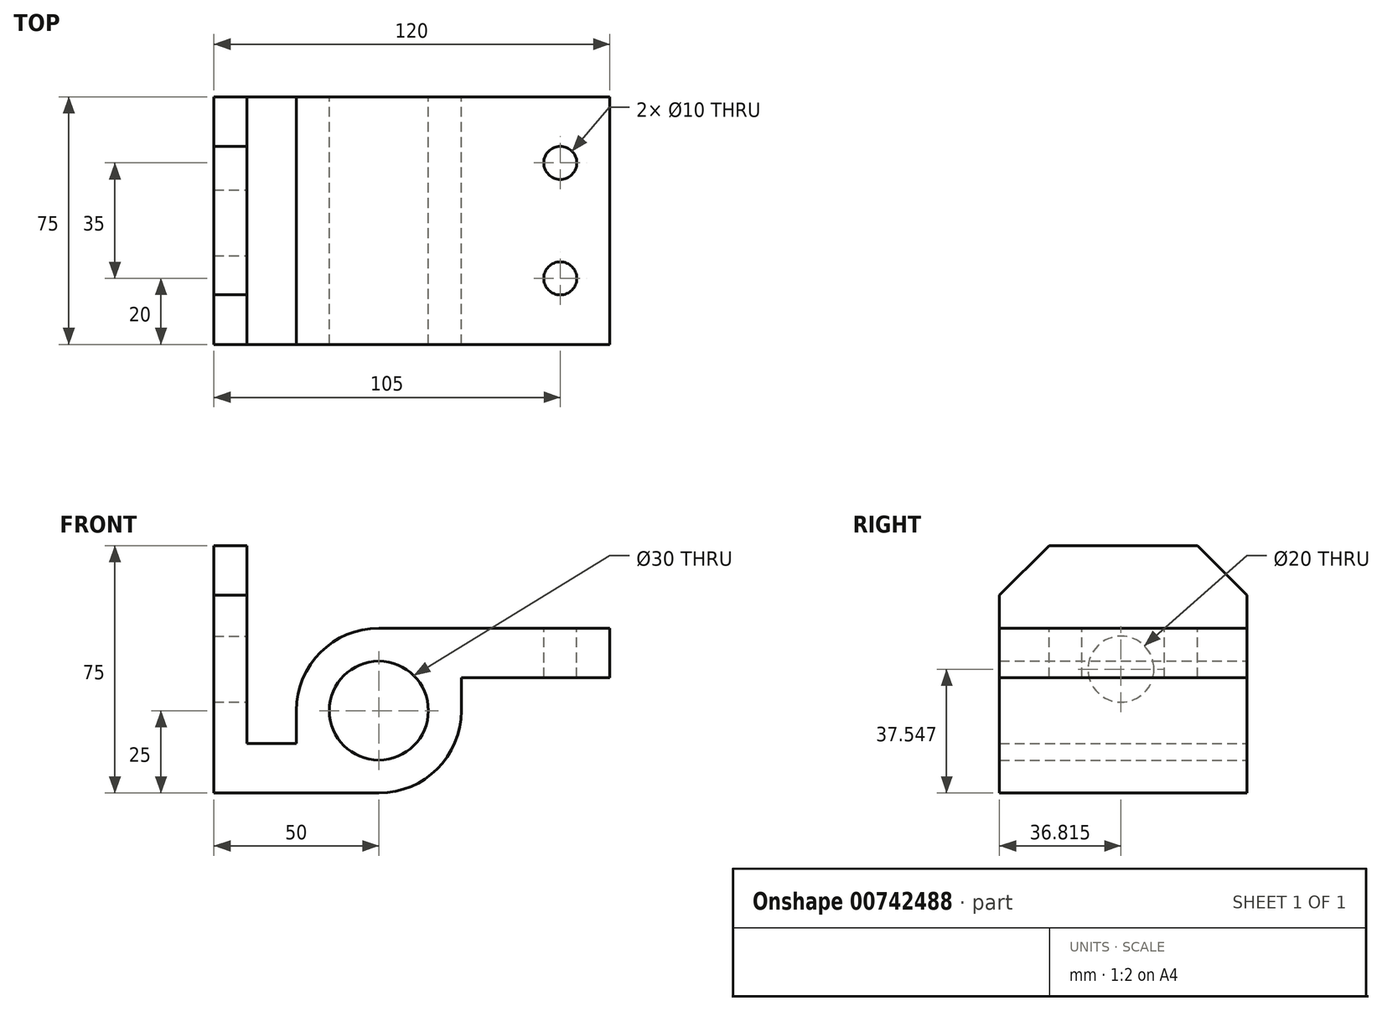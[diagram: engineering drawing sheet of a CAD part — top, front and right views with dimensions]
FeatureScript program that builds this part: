
annotation { "Feature Type Name" : "Feature", "Feature Type Description" : "" }
export const myFeature = defineFeature(function(context is Context, id is Id, definition is map)
    precondition{}
    {
        {
            var Q0;
            Q0=qCreatedBy(makeId("Front.planeOp"),FACE);
            var sketch = newSketch(context, id + "F0", { "sketchPlane" : qUnion([Q0])});
            skLineSegment(sketch, "E0", {"start": v(0, 0) * mm, "end": v(-50, 0) * mm});
            skLineSegment(sketch, "E1", {"start": v(-50, 0) * mm, "end": v(-50, 75) * mm});
            skLineSegment(sketch, "E2", {"start": v(-50, 75) * mm, "end": v(-40, 75) * mm});
            skLineSegment(sketch, "E3", {"start": v(-40, 75) * mm, "end": v(-40, 15) * mm});
            skLineSegment(sketch, "E4", {"start": v(-40, 15) * mm, "end": v(-25, 15) * mm});
            skLineSegment(sketch, "E5", {"start": v(0, 10) * mm, "end": v(0, 25) * mm});
            skArc(sketch, "E6", {"start": v(0, 0) * mm, "mid": v(17.68, 7.32) * mm, "end": v(25, 25) * mm});
            skCircle(sketch, "E7", {"center": v(0, 25) * mm, "radius": 15 * mm});
            skLineSegment(sketch, "E8", {"start": v(-25, 15) * mm, "end": v(-25, 25) * mm});
            skLineSegment(sketch, "E9", {"start": v(0, 50) * mm, "end": v(70, 50) * mm});
            skPoint(sketch, "E10.start.orphan", {"position": v(-25, 0) * mm});
            skLineSegment(sketch, "E11", {"start": v(25, 25) * mm, "end": v(25, 35) * mm});
            skLineSegment(sketch, "E12", {"start": v(70, 50) * mm, "end": v(70, 35) * mm});
            skLineSegment(sketch, "E13", {"start": v(25, 35) * mm, "end": v(70, 35) * mm});
            skArc(sketch, "E14.trimOffspring", {"start": v(0, 50) * mm, "mid": v(-17.68, 42.68) * mm, "end": v(-25, 25) * mm});
            skPoint(sketch, "E15.orphan", {"position": v(25, 0) * mm});
            skSolve(sketch);
        }
        {
            var Q0;
            Q0=makeQuery(id+"F0.imprint","IMPRINT",FACE,{"disambiguationData":[TD([[makeQuery(id+"F0.imprint","IMPRINT",EDGE,{"derivedFrom":sQuery(id+"F0.wireOp",EDGE,"E0")}),-1.0]])]});
            extrude(context, id + "F1", {"entities" : qUnion([Q0]), "depth" : 75 * mm, "offsetDistance" : 25 * mm});
        }
        {
            var Q0;
            Q0=makeQuery(id+"F1.opExtrude","SWEPT_FACE",FACE,{"disambiguationData":[OSD([sQuery(id+"F0.wireOp",EDGE,"E9")])]});
            var sketch = newSketch(context, id + "F2", { "sketchPlane" : qUnion([Q0])});
            skCircle(sketch, "E16", {"center": v(55, -55) * mm, "radius": 5 * mm});
            skCircle(sketch, "E17", {"center": v(55, -20) * mm, "radius": 5 * mm});
            skLineSegment(sketch, "E18.0", {"start": v(70, -75) * mm, "end": v(70, 0) * mm, "construction": true});
            skSolve(sketch);
        }
        {
            var Q0;
            Q0=makeQuery(id+"F2.imprint","IMPRINT",FACE,{"disambiguationData":[TD([[makeQuery(id+"F2.imprint","IMPRINT",EDGE,{"derivedFrom":sQuery(id+"F2.wireOp",EDGE,"E17")}),1.0]])]});
            var Q1;
            Q1=makeQuery(id+"F2.imprint","IMPRINT",FACE,{"disambiguationData":[TD([[makeQuery(id+"F2.imprint","IMPRINT",EDGE,{"derivedFrom":sQuery(id+"F2.wireOp",EDGE,"E16")}),1.0]])]});
            extrude(context, id + "F3", {"entities" : qUnion([Q0, Q1]), "operationType" : NewBodyOperationType.REMOVE, "oppositeDirection" : true, "depth" : 25 * mm, "offsetDistance" : 25 * mm});
        }
        {
            var Q0;
            Q0=makeQuery(id+"F1.opExtrude","SWEPT_FACE",FACE,{"disambiguationData":[OSD([sQuery(id+"F0.wireOp",EDGE,"E1")])]});
            var sketch = newSketch(context, id + "F4", { "sketchPlane" : qUnion([Q0])});
            skPoint(sketch, "E19", {"position": v(0, 60) * mm});
            skPoint(sketch, "E20", {"position": v(15, 75) * mm});
            skPoint(sketch, "E21", {"position": v(60, 75) * mm});
            skPoint(sketch, "E22", {"position": v(75, 60) * mm});
            skPoint(sketch, "E23", {"position": v(0, 75) * mm});
            skPoint(sketch, "E24", {"position": v(75, 75) * mm});
            skLineSegment(sketch, "E25", {"start": v(15, 75) * mm, "end": v(0, 60) * mm});
            skLineSegment(sketch, "E26", {"start": v(60, 75) * mm, "end": v(75, 60) * mm});
            skSolve(sketch);
        }
        {
            var Q0;
            {var subQ0=sQuery(id+"F4.wireOp",EDGE,"E25");Q0=makeQuery(id+"F4.imprint","IMPRINT",FACE,{"disambiguationData":[TD([[makeQuery(id+"F4.imprint","IMPRINT",EDGE,{"derivedFrom":subQ0}),-1.0]])]});}
            var Q1;
            {var subQ0=sQuery(id+"F4.wireOp",EDGE,"E26");Q1=makeQuery(id+"F4.imprint","IMPRINT",FACE,{"disambiguationData":[TD([[makeQuery(id+"F4.imprint","IMPRINT",EDGE,{"derivedFrom":subQ0}),1.0]])]});}
            extrude(context, id + "F5", {"entities" : qUnion([Q0, Q1]), "operationType" : NewBodyOperationType.REMOVE, "oppositeDirection" : true, "depth" : 25 * mm, "offsetDistance" : 25 * mm});
        }
        {
            var Q0;
            Q0=makeQuery(id+"F1.opExtrude","SWEPT_FACE",FACE,{"disambiguationData":[OSD([sQuery(id+"F0.wireOp",EDGE,"E3")])]});
            var sketch = newSketch(context, id + "F6", { "sketchPlane" : qUnion([Q0])});
            skSolve(sketch);
        }
        {
            var Q0;
            {var subQ0=sQuery(id+"F0.wireOp",EDGE,"E3");Q0=makeQuery(id+"F6.imprint","IMPRINT",FACE,{"disambiguationData":[TD([[makeQuery(id+"F6.imprint","IMPRINT",EDGE,{"derivedFrom":makeQuery(id+"F1.opExtrude","CAP_EDGE",EDGE,{"disambiguationData":[OSD([subQ0])],"isStart":true})}),-1.0]])]});}
            var sketch = newSketch(context, id + "F7", { "sketchPlane" : qUnion([Q0])});
            skPoint(sketch, "E27", {"position": v(-38.18, 37.55) * mm});
            skPoint(sketch, "E28", {"position": v(-35.78, 72.55) * mm});
            skPoint(sketch, "E29", {"position": v(-73.18, 37.55) * mm});
            skCircle(sketch, "E30", {"center": v(-38.18, 37.55) * mm, "radius": 10 * mm});
            skSolve(sketch);
        }
        {
            var Q0;
            Q0=makeQuery(id+"F7.imprint","IMPRINT",FACE,{"disambiguationData":[TD([[makeQuery(id+"F7.imprint","IMPRINT",EDGE,{"derivedFrom":sQuery(id+"F7.wireOp",EDGE,"E30")}),1.0]])]});
            extrude(context, id + "F8", {"entities" : qUnion([Q0]), "operationType" : NewBodyOperationType.REMOVE, "oppositeDirection" : true, "depth" : 10 * mm, "offsetDistance" : 25 * mm});
        }
    });
